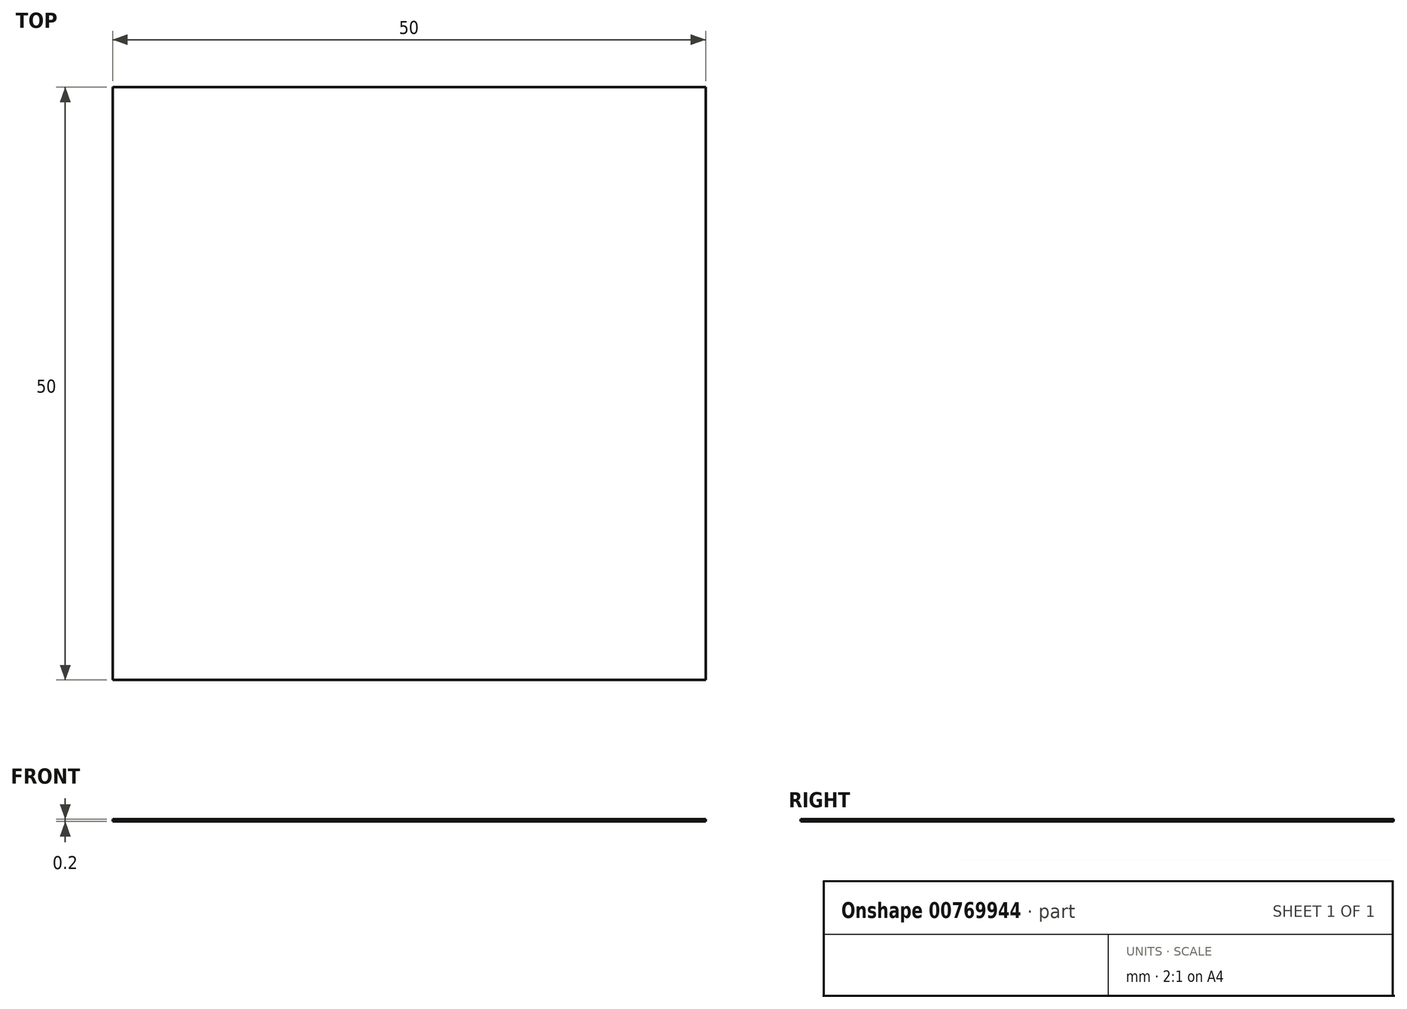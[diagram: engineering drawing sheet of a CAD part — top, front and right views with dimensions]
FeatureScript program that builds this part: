
annotation { "Feature Type Name" : "Feature", "Feature Type Description" : "" }
export const myFeature = defineFeature(function(context is Context, id is Id, definition is map)
    precondition{}
    {
        {
            var Q0;
            Q0=qCreatedBy(makeId("Top.planeOp"),FACE);
            var sketch = newSketch(context, id + "F0", { "sketchPlane" : qUnion([Q0])});
            skLineSegment(sketch, "E0.bottom", {"start": v(25, 25) * mm, "end": v(-25, 25) * mm});
            skLineSegment(sketch, "E0.top", {"start": v(25, -25) * mm, "end": v(-25, -25) * mm});
            skLineSegment(sketch, "E0.left", {"start": v(25, 25) * mm, "end": v(25, -25) * mm});
            skLineSegment(sketch, "E0.right", {"start": v(-25, 25) * mm, "end": v(-25, -25) * mm});
            skPoint(sketch, "E0.middle", {"position": v(0, 0) * mm});
            skSolve(sketch);
        }
        {
            var Q0;
            Q0 = qSketchRegion(id + "F0", true);
            extrude(context, id + "F1", {"entities" : qUnion([Q0]), "depth" : .2 * mm, "offsetDistance" : 25 * mm});
        }
    });
